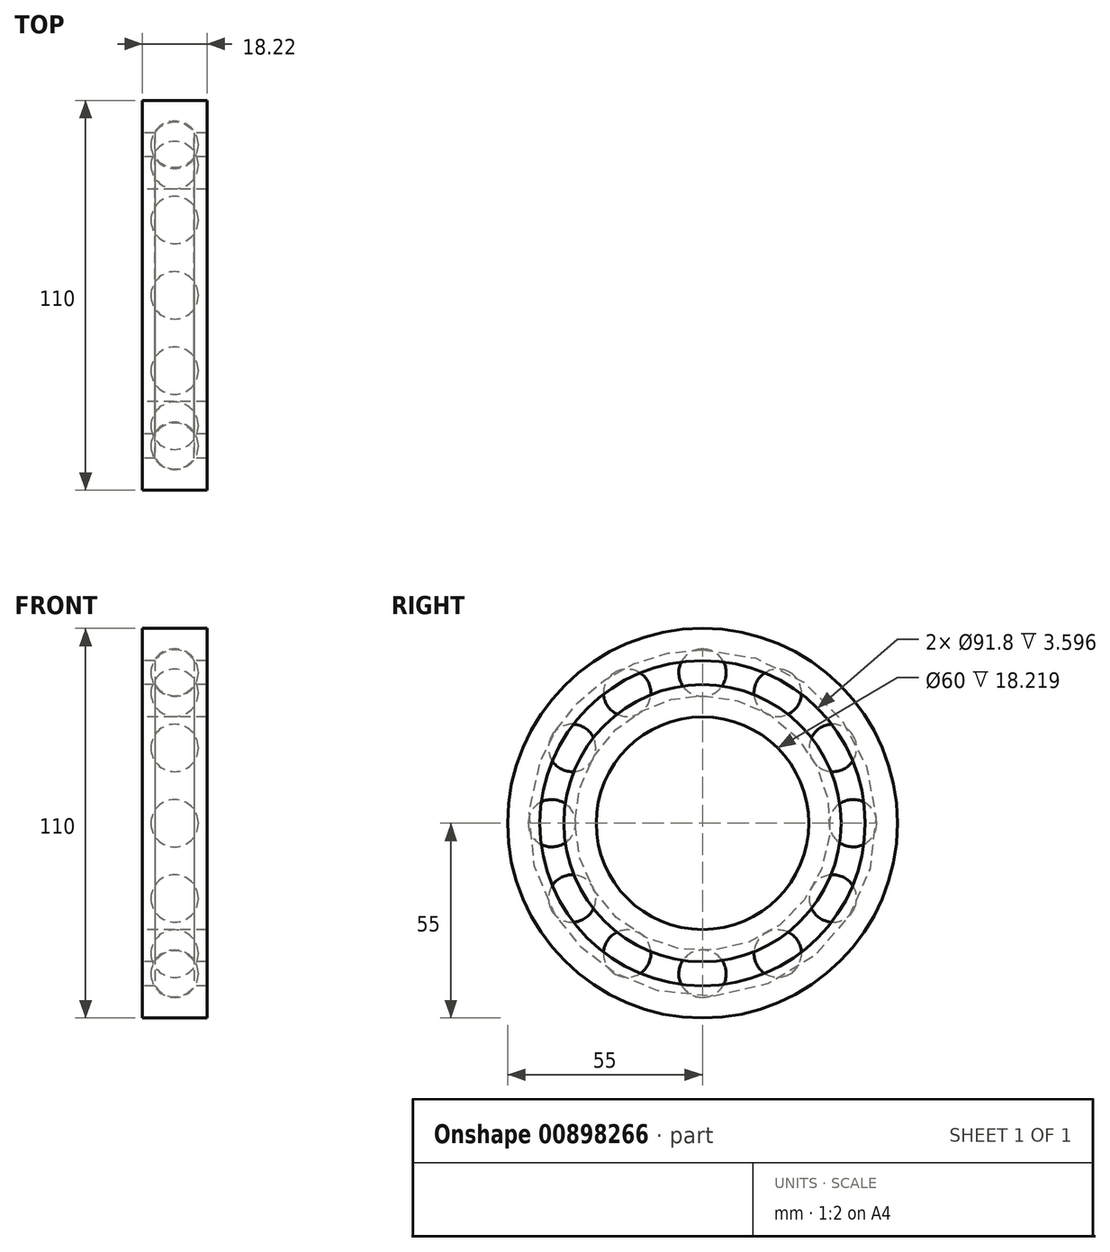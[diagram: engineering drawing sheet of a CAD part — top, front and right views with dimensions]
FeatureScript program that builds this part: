
annotation { "Feature Type Name" : "Feature", "Feature Type Description" : "" }
export const myFeature = defineFeature(function(context is Context, id is Id, definition is map)
    precondition{}
    {
        {
            var Q0;
            Q0=qCreatedBy(makeId("Front.planeOp"),FACE);
            var sketch = newSketch(context, id + "F0", { "sketchPlane" : qUnion([Q0])});
            skLineSegment(sketch, "E0.bottom", {"start": v(9.1, 55) * mm, "end": v(-9.1, 55) * mm});
            skLineSegment(sketch, "E0.top", {"start": v(9.1, 45.9) * mm, "end": v(5.51, 45.9) * mm});
            skLineSegment(sketch, "E0.left", {"start": v(9.1, 55) * mm, "end": v(9.1, 45.9) * mm});
            skLineSegment(sketch, "E0.right", {"start": v(-9.1, 55) * mm, "end": v(-9.1, 45.9) * mm});
            skPoint(sketch, "E0.middle", {"position": v(0, 50.45) * mm});
            skLineSegment(sketch, "E1.bottom", {"start": v(9.1, 39.1) * mm, "end": v(5.51, 39.1) * mm});
            skLineSegment(sketch, "E1.top", {"start": v(9.1, 30) * mm, "end": v(-9.1, 30) * mm});
            skLineSegment(sketch, "E1.left", {"start": v(9.1, 39.1) * mm, "end": v(9.1, 30) * mm});
            skLineSegment(sketch, "E1.right", {"start": v(-9.1, 39.1) * mm, "end": v(-9.1, 30) * mm});
            skPoint(sketch, "E1.middle", {"position": v(0, 34.55) * mm});
            skLineSegment(sketch, "E2", {"start": v(-21.95, 0) * mm, "end": v(18.69, 0) * mm, "construction": true});
            skLineSegment(sketch, "E3", {"start": v(0, 50.45) * mm, "end": v(0, 34.55) * mm, "construction": true});
            skArc(sketch, "E4", {"start": v(-5.51, 39.1) * mm, "mid": v(0, 36.02) * mm, "end": v(5.51, 39.1) * mm});
            skLineSegment(sketch, "E5.trimOffspring", {"start": v(-5.51, 45.9) * mm, "end": v(-9.1, 45.9) * mm});
            skLineSegment(sketch, "E6.trimOffspring", {"start": v(-5.51, 39.1) * mm, "end": v(-9.1, 39.1) * mm});
            skArc(sketch, "E7.trimOffspring", {"start": v(5.51, 45.9) * mm, "mid": v(0, 48.98) * mm, "end": v(-5.51, 45.9) * mm});
            skSolve(sketch);
        }
        {
            var Q0;
            Q0=makeQuery(id+"F0.imprint","IMPRINT",FACE,{"disambiguationData":[TD([[makeQuery(id+"F0.imprint","IMPRINT",EDGE,{"derivedFrom":sQuery(id+"F0.wireOp",EDGE,"E0.bottom")}),1.0]])]});
            var Q1;
            Q1=makeQuery(id+"F0.imprint","IMPRINT",FACE,{"disambiguationData":[TD([[makeQuery(id+"F0.imprint","IMPRINT",EDGE,{"derivedFrom":sQuery(id+"F0.wireOp",EDGE,"E1.bottom")}),1.0]])]});
            var Q2;
            Q2=sQuery(id+"F0.wireOp",EDGE,"E2");
            revolve(context, id + "F1", {"surfaceOperationType" : NewSurfaceOperationType.NEW, "entities" : qUnion([Q0, Q1]), "axis" : qUnion([Q2]), "revolveType" : RevolveType.FULL});
        }
        {
            var Q0;
            Q0=qCreatedBy(makeId("Front.planeOp"),FACE);
            var sketch = newSketch(context, id + "F2", { "sketchPlane" : qUnion([Q0])});
            skArc(sketch, "E8", {"start": v(6.69, 42.5) * mm, "mid": v(0, 49.19) * mm, "end": v(-6.69, 42.5) * mm});
            skLineSegment(sketch, "E9", {"start": v(-6.69, 42.5) * mm, "end": v(6.69, 42.5) * mm});
            skSolve(sketch);
        }
        {
            var Q0;
            Q0=makeQuery(id+"F2.imprint","IMPRINT",FACE,{"disambiguationData":[TD([[makeQuery(id+"F2.imprint","IMPRINT",EDGE,{"derivedFrom":sQuery(id+"F2.wireOp",EDGE,"E8")}),1.0]])]});
            var Q1;
            Q1=sQuery(id+"F2.wireOp",EDGE,"E9");
            revolve(context, id + "F3", {"surfaceOperationType" : NewSurfaceOperationType.NEW, "entities" : qUnion([Q0]), "axis" : qUnion([Q1]), "revolveType" : RevolveType.FULL});
        }
        {
            var Q0;
            Q0=makeQuery(id+"F3.opRevolve","SWEPT_BODY",BODY,{"disambiguationData":[OSD([sQuery(id+"F2.wireOp",EDGE,"E8"),sQuery(id+"F2.wireOp",EDGE,"E9")])]});
            var Q1;
            Q1=makeQuery(id+"F1.opRevolve","SWEPT_EDGE",EDGE,{"disambiguationData":[OSD([sQuery(id+"F0.wireOp",EDGE,"E0.top"),sQuery(id+"F0.wireOp",EDGE,"E0.left")])]});
            circularPattern(context, id + "F4", {"entities" : qUnion([Q0]), "axis" : qUnion([Q1]), "angle" : 360 * degree, "instanceCount" : 12, "equalSpace" : true});
        }
    });
